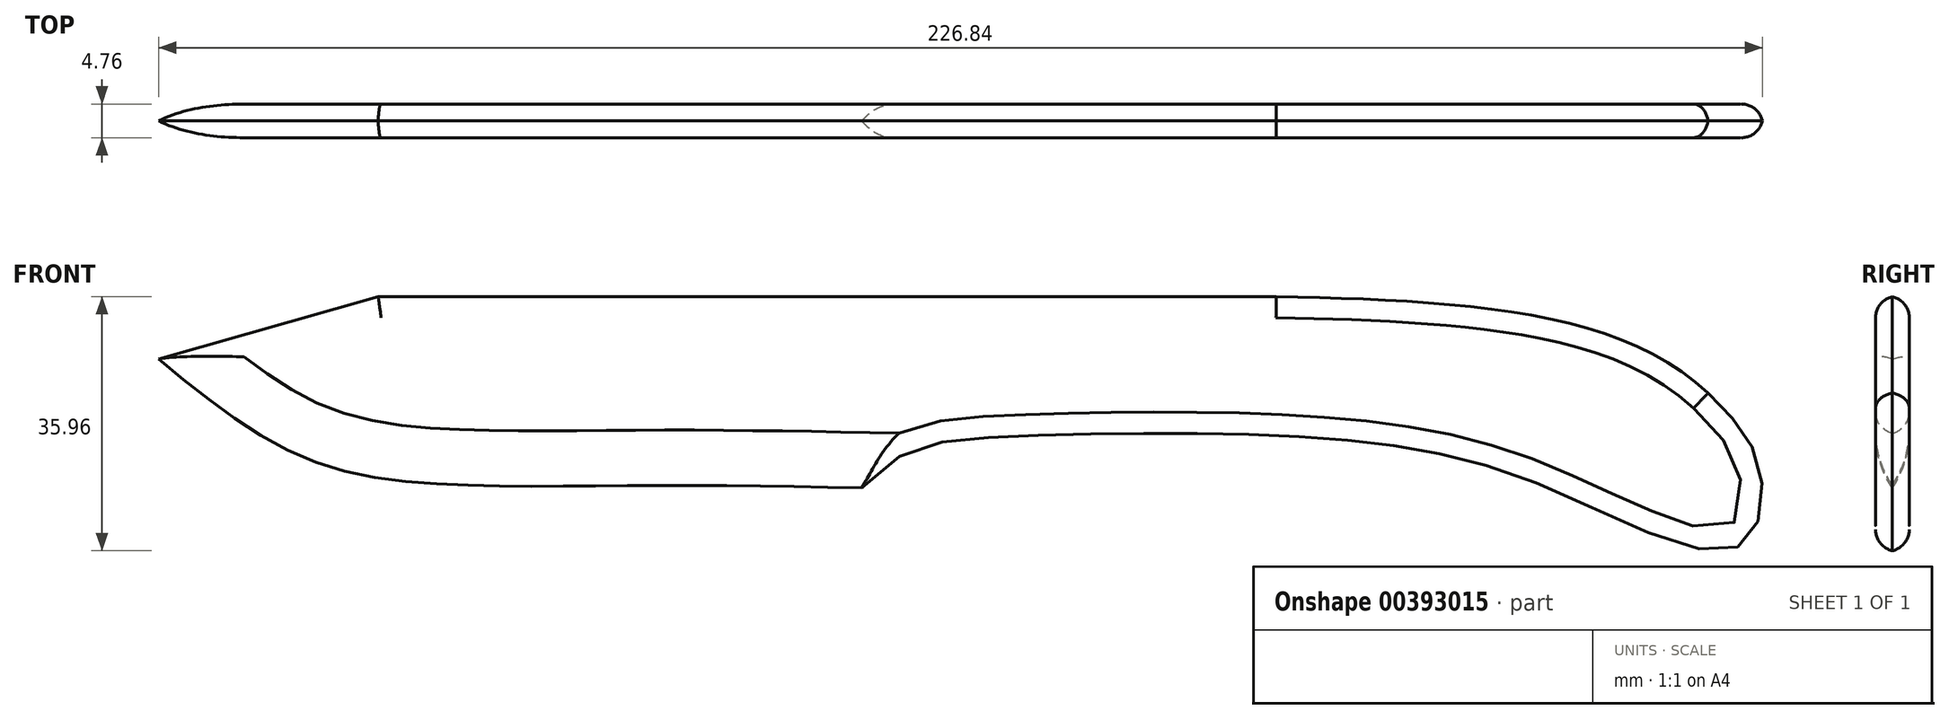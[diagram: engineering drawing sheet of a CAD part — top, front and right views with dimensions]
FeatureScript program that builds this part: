
annotation { "Feature Type Name" : "Feature", "Feature Type Description" : "" }
export const myFeature = defineFeature(function(context is Context, id is Id, definition is map)
    precondition{}
    {
        {
            var Q0;
            Q0=qCreatedBy(makeId("Front.planeOp"),FACE);
            var sketch = newSketch(context, id + "F0", { "sketchPlane" : qUnion([Q0])});
            skLineSegment(sketch, "E0", {"start": v(53.15, 33.14) * mm, "end": v(-73.85, 33.14) * mm});
            skLineSegment(sketch, "E1", {"start": v(-73.85, 33.14) * mm, "end": v(-104.92, 24.33) * mm});
            skFitSpline(sketch, "E2", {"points": [v(-104.92, 24.33) * mm, v(-84.07, 10.24) * mm, v(-60.28, 6.42) * mm, v(-34.14, 6.42) * mm, v(-5.45, 6.1) * mm], "startDerivative": vector(81.3, -67.4) * mm, "endDerivative": vector(110.72, -1.84) * mm});
            skFitSpline(sketch, "E3", {"points": [v(53.15, 33.14) * mm, v(90.9, 30.2) * mm, v(114.24, 19.5) * mm], "startDerivative": vector(70.2, -1.35) * mm, "endDerivative": vector(40.5, -38) * mm});
            skFitSpline(sketch, "E4", {"points": [v(114.24, 19.5) * mm, v(121.4, 9.36) * mm, v(118.44, -2.25) * mm, v(91.52, 6.1) * mm, v(67.56, 12.33) * mm, v(42.52, 13.8) * mm, v(14.47, 13.31) * mm, v(-5.45, 6.1) * mm], "startDerivative": vector(82.11, -79.1) * mm, "endDerivative": vector(-114.34, -137.84) * mm});
            skSolve(sketch);
        }
        {
            var Q0;
            Q0=makeQuery(id+"F0.imprint","IMPRINT",FACE,{"disambiguationData":[TD([[makeQuery(id+"F0.imprint","IMPRINT",EDGE,{"derivedFrom":sQuery(id+"F0.wireOp",EDGE,"E0")}),1.0]])]});
            extrude(context, id + "F1", {"entities" : qUnion([Q0]), "depth" : 2.38 * mm});
        }
        {
            var Q0;
            Q0=makeQuery(id+"F1.opExtrude","CAP_EDGE",EDGE,{"disambiguationData":[OSD([sQuery(id+"F0.wireOp",EDGE,"E2")])],"isStart":false});
            fillet(context, id + "F2", {"entities" : qUnion([Q0]), "radius" : 14.1 * mm, "tangentPropagation" : true, "allowEdgeOverflow" : false});
        }
        {
            var Q0;
            Q0=makeQuery(id+"F1.opExtrude","CAP_EDGE",EDGE,{"disambiguationData":[OSD([sQuery(id+"F0.wireOp",EDGE,"E1")])],"isStart":false});
            fillet(context, id + "F3", {"entities" : qUnion([Q0]), "radius" : 3.07 * mm, "tangentPropagation" : true, "allowEdgeOverflow" : false});
        }
        {
            var Q0;
            Q0=makeQuery(id+"F1.opExtrude","CAP_EDGE",EDGE,{"disambiguationData":[OSD([sQuery(id+"F0.wireOp",EDGE,"E0")])],"isStart":false});
            var Q1;
            Q1=makeQuery(id+"F1.opExtrude","CAP_EDGE",EDGE,{"disambiguationData":[OSD([sQuery(id+"F0.wireOp",EDGE,"E3")])],"isStart":false});
            var Q2;
            Q2=makeQuery(id+"F1.opExtrude","CAP_EDGE",EDGE,{"disambiguationData":[OSD([sQuery(id+"F0.wireOp",EDGE,"E4")])],"isStart":false});
            fillet(context, id + "F4", {"entities" : qUnion([Q0, Q1, Q2]), "radius" : 3.07 * mm, "tangentPropagation" : true, "allowEdgeOverflow" : false});
        }
        {
            var Q0;
            Q0=makeQuery(id+"F1.opExtrude","SWEPT_BODY",BODY,{"disambiguationData":[OSD([sQuery(id+"F0.wireOp",EDGE,"E0"),sQuery(id+"F0.wireOp",EDGE,"E1"),sQuery(id+"F0.wireOp",EDGE,"E2"),sQuery(id+"F0.wireOp",EDGE,"E3"),sQuery(id+"F0.wireOp",EDGE,"E4")])]});
            transform(context, id + "F5", {"entities" : qUnion([Q0]), "transformType" : TransformType.COPY});
        }
        {
            var Q0;
            Q0=makeQuery(id+"F5.opPattern","COPY",BODY,{"derivedFrom":makeQuery(id+"F1.opExtrude","SWEPT_BODY",BODY,{"disambiguationData":[OSD([sQuery(id+"F0.wireOp",EDGE,"E0"),sQuery(id+"F0.wireOp",EDGE,"E1"),sQuery(id+"F0.wireOp",EDGE,"E2"),sQuery(id+"F0.wireOp",EDGE,"E3"),sQuery(id+"F0.wireOp",EDGE,"E4")])]}),"instanceName":"1"});
            var Q1;
            Q1=makeQuery(id+"F1.opExtrude","CAP_FACE",FACE,{"disambiguationData":[OSD([sQuery(id+"F0.wireOp",EDGE,"E0"),sQuery(id+"F0.wireOp",EDGE,"E1"),sQuery(id+"F0.wireOp",EDGE,"E2"),sQuery(id+"F0.wireOp",EDGE,"E3"),sQuery(id+"F0.wireOp",EDGE,"E4")])],"isStart":true});
            mirror(context, id + "F6", {"entities" : qUnion([Q0]), "mirrorPlane" : qUnion([Q1])});
        }
    });
